# Revit family: 859-001X-001 DN350-600 final
name_source: partatom
category: Pipe Accessories
units: mm (PartAtom-declared; Revit-internal decimal feet)

## family parameters
Always vertical = Yes
Cut with Voids When Loaded = No
Part Type = Valve - Breaks Into
Round Connector Dimension = Use Diameter
Shared = No
Work Plane-Based = No

## types (35) — shared parameters
10 = 10 mm  [stored 0.0328084 ft]
131 = 131 mm
18 = 11 mm  [stored 0.0360892 ft]
3 = 3 mm  [stored 0.00984252 ft]
48 = 15 mm  [stored 0.0492126 ft]
50 = 50 mm
53 = 20 mm  [stored 0.0656168 ft]
8 = 8 mm  [stored 0.0262467 ft]
DN350_PN10_Pilot range ( 0.3 - 1.5) = 859-0350-00-0140018
DN350_PN10_Pilot range ( 1.5 - 6) = 859-0350-00-0140010
DN350_PN10_Pilot range ( 5 - 10) = 859-0350-00-0140011
DN350_PN16_Pilot range ( 0.3 - 1.5) = 859-0350-00-1140018
DN350_PN16_Pilot range ( 0.5 - 6) = 859-0350-00-1140010
DN350_PN16_Pilot range ( 10 - 16) = 859-0350-00-1140012
DN350_PN16_Pilot range ( 5 - 10) = 859-0350-00-1140011
DN400_PN10_Pilot range ( 0.3 - 1.5) = 859-0400-00-0140018
DN400_PN10_Pilot range ( 1.5 - 6) = 859-0400-00-0140010
DN400_PN10_Pilot range ( 5 - 10) = 859-0400-00-0140011
DN400_PN16_Pilot range ( 0.3 - 1.5) = 859-0400-00-1140018
DN400_PN16_Pilot range ( 1.5 - 6) = 859-0400-00-1140010
DN400_PN16_Pilot range ( 10 - 16) = 859-0400-00-1140012
DN400_PN16_Pilot range ( 5 - 10) = 859-0400-00-1140011
DN450_PN10_Pilot range ( 0.3 - 1.5) = 859-0450-00-0140018
DN450_PN10_Pilot range ( 1.5 - 6) = 859-0450-00-0140010
DN450_PN10_Pilot range ( 5 - 10) = 859-0450-00-0140011
DN450_PN16_Pilot range (  10 - 16) = 859-0450-00-1140012
DN450_PN16_Pilot range ( 0.3 - 1.5) = 859-0450-00-1140018
DN450_PN16_Pilot range ( 1.5 - 6) = 859-0450-00-1140010
DN450_PN16_Pilot range ( 5 - 10) = 859-0450-00-1140011
DN500_PN10_Pilot range ( 0.3 - 1.5) = 859-0500-00-0140018
DN500_PN10_Pilot range ( 1.5 - 6) = 859-0500-00-0140010
DN500_PN10_Pilot range ( 5 - 10) = 859-0500-00-0140011
DN500_PN16_Pilot range ( 0.3 - 1.5) = 859-0500-00-1140018
DN500_PN16_Pilot range ( 1.5 - 6) = 859-0500-00-1140010
DN500_PN16_Pilot range ( 10 - 16) = 859-0500-00-1140012
DN500_PN16_Pilot range ( 5 - 10) = 859-0500-00-1140011
DN600_PN10_Pilot range ( 0.3 - 1.5) = 859-0600-00-0140018
DN600_PN10_Pilot range ( 1.5 - 6) = 859-0600-00-0140010
DN600_PN10_Pilot range ( 5 - 10) = 859-0600-00-0140011
DN600_PN16_Pilot range ( 0.3 - 1.5) = 859-0600-00-1140018
DN600_PN16_Pilot range ( 1.5 - 6) = 859-0600-00-1140010
DN600_PN16_Pilot range ( 10 - 16) = 859-0600-00-1140012
DN600_PN16_Pilot range ( 5 - 10) = 859-0600-00-1140011
Description_ = AVK CONTROL VALVE, PRESSURE SUSTAINING/RELIEF, PN10/16
Search_table = 859-001X-001 DN350-600
URL_product_pages = https://www.avkvalves.com
zero-valued in all types: 0, Actuator, Default Elevation

## per-type parameters (varying)
- DN350_PN10_Pilot range ( 1.5 - 6): Actuator_L=136 mm; Actuator_L1=122 mm; Actuator_d=43 mm; Body_H=312 mm; Body_Rib_L=130 mm; Bolt_Dia=33 mm  [stored 0.108268 ft]; Bonnet_D=156 mm; Bonnet_D1=312 mm; Bonnet_R=328 mm; Bonnet_dim1=218 mm; Bonnet_dim1_H=22 mm; Bonnet_dim1_H1=445 mm; Bonnet_dim2=109 mm; Bonnet_dim3=82 mm; Bore=175 mm; Bore1=210 mm; Bore2=263 mm; Centre_D=70 mm; Centre_D1=56 mm; Centre_nut=53 mm; Conrol_dim.=186 mm; Control_dim1=16 mm  [stored 0.0524934 ft]; Control_dim2=98 mm; Control_dim3=8 mm  [stored 0.0262467 ft]; Control_dim4=281 mm; Control_dim5=22 mm; Control_dim6=27 mm; Control_dim7=36 mm  [stored 0.11811 ft]; D=260 mm; DN=350 mm; FL_T=25 mm  [stored 0.082021 ft]; H3=808 mm; H33=31 mm; H4=62 mm; L=980 mm; L3=360 mm; Nut_Dim1=42 mm; Nut_Dim2=7 mm  [stored 0.0229659 ft]; Nut_T=20 mm  [stored 0.0656168 ft]; Raised_R=34 mm; Raised_dis=4 mm  [stored 0.0131234 ft]; Sweep_R=19 mm  [stored 0.062336 ft]; Thickness=15 mm  [stored 0.0492126 ft]; Thickness1=18 mm  [stored 0.0590551 ft]; W=290 mm; W1=302 mm; W11=216 mm; W2=302 mm; W22=242 mm; Wd1=257 mm; Wd2=302 mm; centre=273 mm; dim1=121 mm; nut_dim=156 mm; sweep=28 mm  [stored 0.0918635 ft]; sweep/2=6 mm  [stored 0.019685 ft]; sweep1=13 mm; sweep_2=6 mm  [stored 0.019685 ft]; sweep_D=25 mm  [stored 0.082021 ft]; sweep_H=356 mm; sweep_H1=31 mm; sweep_box1=35 mm  [stored 0.114829 ft]; sweep_box2=16 mm  [stored 0.0524934 ft]
- DN350_PN10_Pilot range ( 5 - 10): Actuator_L=136 mm; Actuator_L1=122 mm; Actuator_d=43 mm; Body_H=312 mm; Body_Rib_L=130 mm; Bolt_Dia=33 mm  [stored 0.108268 ft]; Bonnet_D=156 mm; Bonnet_D1=312 mm; Bonnet_R=328 mm; Bonnet_dim1=218 mm; Bonnet_dim1_H=22 mm; Bonnet_dim1_H1=445 mm; Bonnet_dim2=109 mm; Bonnet_dim3=82 mm; Bore=175 mm; Bore1=210 mm; Bore2=263 mm; Centre_D=70 mm; Centre_D1=56 mm; Centre_nut=53 mm; Conrol_dim.=186 mm; Control_dim1=16 mm  [stored 0.0524934 ft]; Control_dim2=98 mm; Control_dim3=8 mm  [stored 0.0262467 ft]; Control_dim4=281 mm; Control_dim5=22 mm; Control_dim6=27 mm; Control_dim7=36 mm  [stored 0.11811 ft]; D=260 mm; DN=350 mm; FL_T=25 mm  [stored 0.082021 ft]; H3=808 mm; H33=31 mm; H4=62 mm; L=980 mm; L3=360 mm; Nut_Dim1=42 mm; Nut_Dim2=7 mm  [stored 0.0229659 ft]; Nut_T=20 mm  [stored 0.0656168 ft]; Raised_R=34 mm; Raised_dis=4 mm  [stored 0.0131234 ft]; Sweep_R=19 mm  [stored 0.062336 ft]; Thickness=15 mm  [stored 0.0492126 ft]; Thickness1=18 mm  [stored 0.0590551 ft]; W=290 mm; W1=302 mm; W11=216 mm; W2=302 mm; W22=242 mm; Wd1=257 mm; Wd2=302 mm; centre=273 mm; dim1=121 mm; nut_dim=156 mm; sweep=28 mm  [stored 0.0918635 ft]; sweep/2=6 mm  [stored 0.019685 ft]; sweep1=13 mm; sweep_2=6 mm  [stored 0.019685 ft]; sweep_D=25 mm  [stored 0.082021 ft]; sweep_H=356 mm; sweep_H1=31 mm; sweep_box1=35 mm  [stored 0.114829 ft]; sweep_box2=16 mm  [stored 0.0524934 ft]
- DN350_PN10_Pilot range ( 0.3 - 1.5): Actuator_L=136 mm; Actuator_L1=122 mm; Actuator_d=43 mm; Body_H=312 mm; Body_Rib_L=130 mm; Bolt_Dia=33 mm  [stored 0.108268 ft]; Bonnet_D=156 mm; Bonnet_D1=312 mm; Bonnet_R=328 mm; Bonnet_dim1=218 mm; Bonnet_dim1_H=22 mm; Bonnet_dim1_H1=445 mm; Bonnet_dim2=109 mm; Bonnet_dim3=82 mm; Bore=175 mm; Bore1=210 mm; Bore2=263 mm; Centre_D=70 mm; Centre_D1=56 mm; Centre_nut=53 mm; Conrol_dim.=186 mm; Control_dim1=16 mm  [stored 0.0524934 ft]; Control_dim2=98 mm; Control_dim3=8 mm  [stored 0.0262467 ft]; Control_dim4=281 mm; Control_dim5=22 mm; Control_dim6=27 mm; Control_dim7=36 mm  [stored 0.11811 ft]; D=260 mm; DN=350 mm; FL_T=25 mm  [stored 0.082021 ft]; H3=808 mm; H33=31 mm; H4=62 mm; L=980 mm; L3=360 mm; Nut_Dim1=42 mm; Nut_Dim2=7 mm  [stored 0.0229659 ft]; Nut_T=20 mm  [stored 0.0656168 ft]; Raised_R=34 mm; Raised_dis=4 mm  [stored 0.0131234 ft]; Sweep_R=19 mm  [stored 0.062336 ft]; Thickness=15 mm  [stored 0.0492126 ft]; Thickness1=18 mm  [stored 0.0590551 ft]; W=290 mm; W1=302 mm; W11=216 mm; W2=302 mm; W22=242 mm; Wd1=257 mm; Wd2=302 mm; centre=273 mm; dim1=121 mm; nut_dim=156 mm; sweep=28 mm  [stored 0.0918635 ft]; sweep/2=6 mm  [stored 0.019685 ft]; sweep1=13 mm; sweep_2=6 mm  [stored 0.019685 ft]; sweep_D=25 mm  [stored 0.082021 ft]; sweep_H=356 mm; sweep_H1=31 mm; sweep_box1=35 mm  [stored 0.114829 ft]; sweep_box2=16 mm  [stored 0.0524934 ft]
- DN350_PN16_Pilot range ( 0.5 - 6): Actuator_L=136 mm; Actuator_L1=122 mm; Actuator_d=43 mm; Body_H=312 mm; Body_Rib_L=130 mm; Bolt_Dia=33 mm  [stored 0.108268 ft]; Bonnet_D=156 mm; Bonnet_D1=312 mm; Bonnet_R=328 mm; Bonnet_dim1=218 mm; Bonnet_dim1_H=22 mm; Bonnet_dim1_H1=445 mm; Bonnet_dim2=109 mm; Bonnet_dim3=82 mm; Bore=175 mm; Bore1=210 mm; Bore2=263 mm; Centre_D=70 mm; Centre_D1=56 mm; Centre_nut=53 mm; Conrol_dim.=186 mm; Control_dim1=16 mm  [stored 0.0524934 ft]; Control_dim2=98 mm; Control_dim3=8 mm  [stored 0.0262467 ft]; Control_dim4=281 mm; Control_dim5=22 mm; Control_dim6=27 mm; Control_dim7=36 mm  [stored 0.11811 ft]; D=260 mm; DN=351 mm; FL_T=27 mm; H3=808 mm; H33=31 mm; H4=62 mm; L=980 mm; L3=360 mm; Nut_Dim1=42 mm; Nut_Dim2=7 mm  [stored 0.0229659 ft]; Nut_T=21 mm; Raised_R=34 mm; Raised_dis=4 mm  [stored 0.0131234 ft]; Sweep_R=19 mm  [stored 0.062336 ft]; Thickness=16 mm  [stored 0.0524934 ft]; Thickness1=19 mm  [stored 0.062336 ft]; W=290 mm; W1=302 mm; W11=216 mm; W2=302 mm; W22=242 mm; Wd1=257 mm; Wd2=302 mm; centre=273 mm; dim1=121 mm; nut_dim=156 mm; sweep=28 mm  [stored 0.0918635 ft]; sweep/2=6 mm  [stored 0.019685 ft]; sweep1=13 mm; sweep_2=6 mm  [stored 0.019685 ft]; sweep_D=25 mm  [stored 0.082021 ft]; sweep_H=356 mm; sweep_H1=31 mm; sweep_box1=35 mm  [stored 0.114829 ft]; sweep_box2=16 mm  [stored 0.0524934 ft]
- DN350_PN16_Pilot range ( 5 - 10): Actuator_L=136 mm; Actuator_L1=122 mm; Actuator_d=43 mm; Body_H=312 mm; Body_Rib_L=130 mm; Bolt_Dia=33 mm  [stored 0.108268 ft]; Bonnet_D=156 mm; Bonnet_D1=312 mm; Bonnet_R=328 mm; Bonnet_dim1=218 mm; Bonnet_dim1_H=22 mm; Bonnet_dim1_H1=445 mm; Bonnet_dim2=109 mm; Bonnet_dim3=82 mm; Bore=175 mm; Bore1=210 mm; Bore2=263 mm; Centre_D=70 mm; Centre_D1=56 mm; Centre_nut=53 mm; Conrol_dim.=186 mm; Control_dim1=16 mm  [stored 0.0524934 ft]; Control_dim2=98 mm; Control_dim3=8 mm  [stored 0.0262467 ft]; Control_dim4=281 mm; Control_dim5=22 mm; Control_dim6=27 mm; Control_dim7=36 mm  [stored 0.11811 ft]; D=260 mm; DN=351 mm; FL_T=27 mm; H3=808 mm; H33=31 mm; H4=62 mm; L=980 mm; L3=360 mm; Nut_Dim1=42 mm; Nut_Dim2=7 mm  [stored 0.0229659 ft]; Nut_T=21 mm; Raised_R=34 mm; Raised_dis=4 mm  [stored 0.0131234 ft]; Sweep_R=19 mm  [stored 0.062336 ft]; Thickness=16 mm  [stored 0.0524934 ft]; Thickness1=19 mm  [stored 0.062336 ft]; W=290 mm; W1=302 mm; W11=216 mm; W2=302 mm; W22=242 mm; Wd1=257 mm; Wd2=302 mm; centre=274 mm; dim1=121 mm; nut_dim=156 mm; sweep=28 mm  [stored 0.0918635 ft]; sweep/2=6 mm  [stored 0.019685 ft]; sweep1=13 mm; sweep_2=6 mm  [stored 0.019685 ft]; sweep_D=25 mm  [stored 0.082021 ft]; sweep_H=356 mm; sweep_H1=31 mm; sweep_box1=35 mm  [stored 0.114829 ft]; sweep_box2=16 mm  [stored 0.0524934 ft]
- DN350_PN16_Pilot range ( 10 - 16): Actuator_L=136 mm; Actuator_L1=122 mm; Actuator_d=43 mm; Body_H=312 mm; Body_Rib_L=130 mm; Bolt_Dia=33 mm  [stored 0.108268 ft]; Bonnet_D=156 mm; Bonnet_D1=312 mm; Bonnet_R=328 mm; Bonnet_dim1=218 mm; Bonnet_dim1_H=22 mm; Bonnet_dim1_H1=445 mm; Bonnet_dim2=109 mm; Bonnet_dim3=82 mm; Bore=175 mm; Bore1=210 mm; Bore2=263 mm; Centre_D=70 mm; Centre_D1=56 mm; Centre_nut=53 mm; Conrol_dim.=186 mm; Control_dim1=16 mm  [stored 0.0524934 ft]; Control_dim2=98 mm; Control_dim3=8 mm  [stored 0.0262467 ft]; Control_dim4=281 mm; Control_dim5=22 mm; Control_dim6=27 mm; Control_dim7=36 mm  [stored 0.11811 ft]; D=260 mm; DN=351 mm; FL_T=27 mm; H3=808 mm; H33=31 mm; H4=62 mm; L=980 mm; L3=360 mm; Nut_Dim1=42 mm; Nut_Dim2=7 mm  [stored 0.0229659 ft]; Nut_T=21 mm; Raised_R=34 mm; Raised_dis=4 mm  [stored 0.0131234 ft]; Sweep_R=19 mm  [stored 0.062336 ft]; Thickness=16 mm  [stored 0.0524934 ft]; Thickness1=19 mm  [stored 0.062336 ft]; W=290 mm; W1=302 mm; W11=216 mm; W2=302 mm; W22=242 mm; Wd1=257 mm; Wd2=302 mm; centre=273 mm; dim1=121 mm; nut_dim=156 mm; sweep=28 mm  [stored 0.0918635 ft]; sweep/2=6 mm  [stored 0.019685 ft]; sweep1=13 mm; sweep_2=6 mm  [stored 0.019685 ft]; sweep_D=25 mm  [stored 0.082021 ft]; sweep_H=356 mm; sweep_H1=31 mm; sweep_box1=35 mm  [stored 0.114829 ft]; sweep_box2=16 mm  [stored 0.0524934 ft]
- DN350_PN16_Pilot range ( 0.3 - 1.5): Actuator_L=136 mm; Actuator_L1=122 mm; Actuator_d=43 mm; Body_H=312 mm; Body_Rib_L=130 mm; Bolt_Dia=33 mm  [stored 0.108268 ft]; Bonnet_D=156 mm; Bonnet_D1=312 mm; Bonnet_R=328 mm; Bonnet_dim1=218 mm; Bonnet_dim1_H=22 mm; Bonnet_dim1_H1=445 mm; Bonnet_dim2=109 mm; Bonnet_dim3=82 mm; Bore=175 mm; Bore1=210 mm; Bore2=263 mm; Centre_D=70 mm; Centre_D1=56 mm; Centre_nut=53 mm; Conrol_dim.=186 mm; Control_dim1=16 mm  [stored 0.0524934 ft]; Control_dim2=98 mm; Control_dim3=8 mm  [stored 0.0262467 ft]; Control_dim4=281 mm; Control_dim5=22 mm; Control_dim6=27 mm; Control_dim7=36 mm  [stored 0.11811 ft]; D=260 mm; DN=350 mm; FL_T=27 mm; H3=808 mm; H33=31 mm; H4=62 mm; L=980 mm; L3=360 mm; Nut_Dim1=42 mm; Nut_Dim2=7 mm  [stored 0.0229659 ft]; Nut_T=21 mm; Raised_R=34 mm; Raised_dis=4 mm  [stored 0.0131234 ft]; Sweep_R=19 mm  [stored 0.062336 ft]; Thickness=16 mm  [stored 0.0524934 ft]; Thickness1=19 mm  [stored 0.062336 ft]; W=290 mm; W1=302 mm; W11=216 mm; W2=302 mm; W22=242 mm; Wd1=257 mm; Wd2=302 mm; centre=273 mm; dim1=121 mm; nut_dim=156 mm; sweep=28 mm  [stored 0.0918635 ft]; sweep/2=6 mm  [stored 0.019685 ft]; sweep1=13 mm; sweep_2=6 mm  [stored 0.019685 ft]; sweep_D=25 mm  [stored 0.082021 ft]; sweep_H=356 mm; sweep_H1=31 mm; sweep_box1=35 mm  [stored 0.114829 ft]; sweep_box2=16 mm  [stored 0.0524934 ft]
- DN400_PN10_Pilot range ( 1.5 - 6): Actuator_L=160 mm; Actuator_L1=144 mm; Actuator_d=48 mm; Body_H=348 mm; Body_Rib_L=145 mm; Bolt_Dia=39 mm  [stored 0.127953 ft]; Bonnet_D=174 mm; Bonnet_D1=348 mm; Bonnet_R=365 mm; Bonnet_dim1=244 mm; Bonnet_dim1_H=35 mm  [stored 0.114829 ft]; Bonnet_dim1_H1=522 mm; Bonnet_dim2=122 mm; Bonnet_dim3=91 mm; Bore=200 mm; Bore1=240 mm; Bore2=300 mm; Centre_D=80 mm; Centre_D1=64 mm; Centre_nut=60 mm; Conrol_dim.=207 mm; Control_dim1=18 mm  [stored 0.0590551 ft]; Control_dim2=110 mm; Control_dim3=9 mm; Control_dim4=313 mm; Control_dim5=25 mm  [stored 0.082021 ft]; Control_dim6=30 mm  [stored 0.0984252 ft]; Control_dim7=40 mm  [stored 0.131234 ft]; D=290 mm; DN=400 mm; FL_T=25 mm  [stored 0.082021 ft]; H3=932 mm; H33=36 mm  [stored 0.11811 ft]; H4=72 mm; L=1100 mm; L3=402 mm; Nut_Dim1=51 mm; Nut_Dim2=7 mm  [stored 0.0229659 ft]; Nut_T=20 mm  [stored 0.0656168 ft]; Raised_R=36 mm  [stored 0.11811 ft]; Raised_dis=4 mm  [stored 0.0131234 ft]; Sweep_R=23 mm; Thickness=15 mm  [stored 0.0492126 ft]; Thickness1=18 mm  [stored 0.0590551 ft]; W=340 mm; W1=355 mm; W11=254 mm; W2=355 mm; W22=284 mm; Wd1=302 mm; Wd2=343 mm; centre=312 mm; dim1=142 mm; nut_dim=174 mm; sweep=33 mm  [stored 0.108268 ft]; sweep/2=8 mm  [stored 0.0262467 ft]; sweep1=15 mm  [stored 0.0492126 ft]; sweep_2=8 mm  [stored 0.0262467 ft]; sweep_D=30 mm  [stored 0.0984252 ft]; sweep_H=417 mm; sweep_H1=49 mm; sweep_box1=40 mm  [stored 0.131234 ft]; sweep_box2=20 mm  [stored 0.0656168 ft]
- DN400_PN10_Pilot range ( 5 - 10): Actuator_L=160 mm; Actuator_L1=144 mm; Actuator_d=48 mm; Body_H=348 mm; Body_Rib_L=145 mm; Bolt_Dia=39 mm  [stored 0.127953 ft]; Bonnet_D=174 mm; Bonnet_D1=348 mm; Bonnet_R=365 mm; Bonnet_dim1=244 mm; Bonnet_dim1_H=35 mm  [stored 0.114829 ft]; Bonnet_dim1_H1=522 mm; Bonnet_dim2=122 mm; Bonnet_dim3=91 mm; Bore=200 mm; Bore1=240 mm; Bore2=300 mm; Centre_D=80 mm; Centre_D1=64 mm; Centre_nut=60 mm; Conrol_dim.=207 mm; Control_dim1=18 mm  [stored 0.0590551 ft]; Control_dim2=110 mm; Control_dim3=9 mm; Control_dim4=313 mm; Control_dim5=25 mm  [stored 0.082021 ft]; Control_dim6=30 mm  [stored 0.0984252 ft]; Control_dim7=40 mm  [stored 0.131234 ft]; D=290 mm; DN=400 mm; FL_T=25 mm  [stored 0.082021 ft]; H3=932 mm; H33=36 mm  [stored 0.11811 ft]; H4=72 mm; L=1100 mm; L3=402 mm; Nut_Dim1=51 mm; Nut_Dim2=7 mm  [stored 0.0229659 ft]; Nut_T=20 mm  [stored 0.0656168 ft]; Raised_R=36 mm  [stored 0.11811 ft]; Raised_dis=4 mm  [stored 0.0131234 ft]; Sweep_R=23 mm; Thickness=15 mm  [stored 0.0492126 ft]; Thickness1=18 mm  [stored 0.0590551 ft]; W=340 mm; W1=355 mm; W11=254 mm; W2=355 mm; W22=284 mm; Wd1=302 mm; Wd2=343 mm; centre=312 mm; dim1=142 mm; nut_dim=174 mm; sweep=33 mm  [stored 0.108268 ft]; sweep/2=8 mm  [stored 0.0262467 ft]; sweep1=15 mm  [stored 0.0492126 ft]; sweep_2=8 mm  [stored 0.0262467 ft]; sweep_D=30 mm  [stored 0.0984252 ft]; sweep_H=417 mm; sweep_H1=49 mm; sweep_box1=40 mm  [stored 0.131234 ft]; sweep_box2=20 mm  [stored 0.0656168 ft]
- DN400_PN10_Pilot range ( 0.3 - 1.5): Actuator_L=160 mm; Actuator_L1=144 mm; Actuator_d=48 mm; Body_H=348 mm; Body_Rib_L=145 mm; Bolt_Dia=39 mm  [stored 0.127953 ft]; Bonnet_D=174 mm; Bonnet_D1=348 mm; Bonnet_R=365 mm; Bonnet_dim1=244 mm; Bonnet_dim1_H=35 mm  [stored 0.114829 ft]; Bonnet_dim1_H1=522 mm; Bonnet_dim2=122 mm; Bonnet_dim3=91 mm; Bore=200 mm; Bore1=240 mm; Bore2=300 mm; Centre_D=80 mm; Centre_D1=64 mm; Centre_nut=60 mm; Conrol_dim.=207 mm; Control_dim1=18 mm  [stored 0.0590551 ft]; Control_dim2=110 mm; Control_dim3=9 mm; Control_dim4=313 mm; Control_dim5=25 mm  [stored 0.082021 ft]; Control_dim6=30 mm  [stored 0.0984252 ft]; Control_dim7=40 mm  [stored 0.131234 ft]; D=290 mm; DN=400 mm; FL_T=25 mm  [stored 0.082021 ft]; H3=932 mm; H33=36 mm  [stored 0.11811 ft]; H4=72 mm; L=1100 mm; L3=402 mm; Nut_Dim1=51 mm; Nut_Dim2=7 mm  [stored 0.0229659 ft]; Nut_T=20 mm  [stored 0.0656168 ft]; Raised_R=36 mm  [stored 0.11811 ft]; Raised_dis=4 mm  [stored 0.0131234 ft]; Sweep_R=23 mm; Thickness=15 mm  [stored 0.0492126 ft]; Thickness1=18 mm  [stored 0.0590551 ft]; W=340 mm; W1=355 mm; W11=254 mm; W2=355 mm; W22=284 mm; Wd1=302 mm; Wd2=343 mm; centre=312 mm; dim1=142 mm; nut_dim=174 mm; sweep=33 mm  [stored 0.108268 ft]; sweep/2=8 mm  [stored 0.0262467 ft]; sweep1=15 mm  [stored 0.0492126 ft]; sweep_2=8 mm  [stored 0.0262467 ft]; sweep_D=30 mm  [stored 0.0984252 ft]; sweep_H=417 mm; sweep_H1=49 mm; sweep_box1=40 mm  [stored 0.131234 ft]; sweep_box2=20 mm  [stored 0.0656168 ft]
- DN400_PN16_Pilot range ( 1.5 - 6): Actuator_L=160 mm; Actuator_L1=144 mm; Actuator_d=48 mm; Body_H=348 mm; Body_Rib_L=145 mm; Bolt_Dia=39 mm  [stored 0.127953 ft]; Bonnet_D=174 mm; Bonnet_D1=348 mm; Bonnet_R=365 mm; Bonnet_dim1=244 mm; Bonnet_dim1_H=35 mm  [stored 0.114829 ft]; Bonnet_dim1_H1=522 mm; Bonnet_dim2=122 mm; Bonnet_dim3=91 mm; Bore=200 mm; Bore1=240 mm; Bore2=300 mm; Centre_D=80 mm; Centre_D1=64 mm; Centre_nut=60 mm; Conrol_dim.=207 mm; Control_dim1=18 mm  [stored 0.0590551 ft]; Control_dim2=110 mm; Control_dim3=9 mm; Control_dim4=313 mm; Control_dim5=25 mm  [stored 0.082021 ft]; Control_dim6=30 mm  [stored 0.0984252 ft]; Control_dim7=40 mm  [stored 0.131234 ft]; D=290 mm; DN=401 mm; FL_T=28 mm  [stored 0.0918635 ft]; H3=932 mm; H33=36 mm  [stored 0.11811 ft]; H4=72 mm; L=1100 mm; L3=402 mm; Nut_Dim1=51 mm; Nut_Dim2=7 mm  [stored 0.0229659 ft]; Nut_T=22 mm; Raised_R=36 mm  [stored 0.11811 ft]; Raised_dis=4 mm  [stored 0.0131234 ft]; Sweep_R=23 mm; Thickness=17 mm; Thickness1=20 mm  [stored 0.0656168 ft]; W=340 mm; W1=355 mm; W11=254 mm; W2=355 mm; W22=284 mm; Wd1=302 mm; Wd2=343 mm; centre=312 mm; dim1=142 mm; nut_dim=174 mm; sweep=33 mm  [stored 0.108268 ft]; sweep/2=8 mm  [stored 0.0262467 ft]; sweep1=15 mm  [stored 0.0492126 ft]; sweep_2=8 mm  [stored 0.0262467 ft]; sweep_D=30 mm  [stored 0.0984252 ft]; sweep_H=417 mm; sweep_H1=49 mm; sweep_box1=40 mm  [stored 0.131234 ft]; sweep_box2=20 mm  [stored 0.0656168 ft]
- DN400_PN16_Pilot range ( 5 - 10): Actuator_L=160 mm; Actuator_L1=144 mm; Actuator_d=48 mm; Body_H=348 mm; Body_Rib_L=145 mm; Bolt_Dia=39 mm  [stored 0.127953 ft]; Bonnet_D=174 mm; Bonnet_D1=348 mm; Bonnet_R=365 mm; Bonnet_dim1=244 mm; Bonnet_dim1_H=35 mm  [stored 0.114829 ft]; Bonnet_dim1_H1=522 mm; Bonnet_dim2=122 mm; Bonnet_dim3=91 mm; Bore=200 mm; Bore1=240 mm; Bore2=301 mm; Centre_D=80 mm; Centre_D1=64 mm; Centre_nut=60 mm; Conrol_dim.=207 mm; Control_dim1=18 mm  [stored 0.0590551 ft]; Control_dim2=110 mm; Control_dim3=9 mm; Control_dim4=313 mm; Control_dim5=25 mm  [stored 0.082021 ft]; Control_dim6=30 mm  [stored 0.0984252 ft]; Control_dim7=40 mm  [stored 0.131234 ft]; D=290 mm; DN=401 mm; FL_T=28 mm  [stored 0.0918635 ft]; H3=932 mm; H33=36 mm  [stored 0.11811 ft]; H4=72 mm; L=1100 mm; L3=402 mm; Nut_Dim1=51 mm; Nut_Dim2=7 mm  [stored 0.0229659 ft]; Nut_T=22 mm; Raised_R=36 mm  [stored 0.11811 ft]; Raised_dis=4 mm  [stored 0.0131234 ft]; Sweep_R=23 mm; Thickness=17 mm; Thickness1=20 mm  [stored 0.0656168 ft]; W=340 mm; W1=355 mm; W11=254 mm; W2=355 mm; W22=284 mm; Wd1=302 mm; Wd2=343 mm; centre=313 mm; dim1=142 mm; nut_dim=174 mm; sweep=33 mm  [stored 0.108268 ft]; sweep/2=8 mm  [stored 0.0262467 ft]; sweep1=15 mm  [stored 0.0492126 ft]; sweep_2=8 mm  [stored 0.0262467 ft]; sweep_D=30 mm  [stored 0.0984252 ft]; sweep_H=417 mm; sweep_H1=49 mm; sweep_box1=40 mm  [stored 0.131234 ft]; sweep_box2=20 mm  [stored 0.0656168 ft]
- DN400_PN16_Pilot range ( 10 - 16): Actuator_L=160 mm; Actuator_L1=144 mm; Actuator_d=48 mm; Body_H=348 mm; Body_Rib_L=145 mm; Bolt_Dia=39 mm  [stored 0.127953 ft]; Bonnet_D=174 mm; Bonnet_D1=348 mm; Bonnet_R=365 mm; Bonnet_dim1=244 mm; Bonnet_dim1_H=35 mm  [stored 0.114829 ft]; Bonnet_dim1_H1=522 mm; Bonnet_dim2=122 mm; Bonnet_dim3=91 mm; Bore=200 mm; Bore1=240 mm; Bore2=300 mm; Centre_D=80 mm; Centre_D1=64 mm; Centre_nut=60 mm; Conrol_dim.=207 mm; Control_dim1=18 mm  [stored 0.0590551 ft]; Control_dim2=110 mm; Control_dim3=9 mm; Control_dim4=313 mm; Control_dim5=25 mm  [stored 0.082021 ft]; Control_dim6=30 mm  [stored 0.0984252 ft]; Control_dim7=40 mm  [stored 0.131234 ft]; D=290 mm; DN=401 mm; FL_T=28 mm  [stored 0.0918635 ft]; H3=932 mm; H33=36 mm  [stored 0.11811 ft]; H4=72 mm; L=1100 mm; L3=402 mm; Nut_Dim1=51 mm; Nut_Dim2=7 mm  [stored 0.0229659 ft]; Nut_T=22 mm; Raised_R=36 mm  [stored 0.11811 ft]; Raised_dis=4 mm  [stored 0.0131234 ft]; Sweep_R=23 mm; Thickness=17 mm; Thickness1=20 mm  [stored 0.0656168 ft]; W=340 mm; W1=355 mm; W11=254 mm; W2=355 mm; W22=284 mm; Wd1=302 mm; Wd2=343 mm; centre=312 mm; dim1=142 mm; nut_dim=174 mm; sweep=33 mm  [stored 0.108268 ft]; sweep/2=8 mm  [stored 0.0262467 ft]; sweep1=15 mm  [stored 0.0492126 ft]; sweep_2=8 mm  [stored 0.0262467 ft]; sweep_D=30 mm  [stored 0.0984252 ft]; sweep_H=417 mm; sweep_H1=49 mm; sweep_box1=40 mm  [stored 0.131234 ft]; sweep_box2=20 mm  [stored 0.0656168 ft]
- DN400_PN16_Pilot range ( 0.3 - 1.5): Actuator_L=160 mm; Actuator_L1=144 mm; Actuator_d=48 mm; Body_H=348 mm; Body_Rib_L=145 mm; Bolt_Dia=39 mm  [stored 0.127953 ft]; Bonnet_D=174 mm; Bonnet_D1=348 mm; Bonnet_R=365 mm; Bonnet_dim1=244 mm; Bonnet_dim1_H=35 mm  [stored 0.114829 ft]; Bonnet_dim1_H1=522 mm; Bonnet_dim2=122 mm; Bonnet_dim3=91 mm; Bore=200 mm; Bore1=240 mm; Bore2=300 mm; Centre_D=80 mm; Centre_D1=64 mm; Centre_nut=60 mm; Conrol_dim.=207 mm; Control_dim1=18 mm  [stored 0.0590551 ft]; Control_dim2=110 mm; Control_dim3=9 mm; Control_dim4=313 mm; Control_dim5=25 mm  [stored 0.082021 ft]; Control_dim6=30 mm  [stored 0.0984252 ft]; Control_dim7=40 mm  [stored 0.131234 ft]; D=290 mm; DN=400 mm; FL_T=28 mm  [stored 0.0918635 ft]; H3=932 mm; H33=36 mm  [stored 0.11811 ft]; H4=72 mm; L=1100 mm; L3=402 mm; Nut_Dim1=51 mm; Nut_Dim2=7 mm  [stored 0.0229659 ft]; Nut_T=22 mm; Raised_R=36 mm  [stored 0.11811 ft]; Raised_dis=4 mm  [stored 0.0131234 ft]; Sweep_R=23 mm; Thickness=17 mm; Thickness1=20 mm  [stored 0.0656168 ft]; W=340 mm; W1=355 mm; W11=254 mm; W2=355 mm; W22=284 mm; Wd1=302 mm; Wd2=343 mm; centre=312 mm; dim1=142 mm; nut_dim=174 mm; sweep=33 mm  [stored 0.108268 ft]; sweep/2=8 mm  [stored 0.0262467 ft]; sweep1=15 mm  [stored 0.0492126 ft]; sweep_2=8 mm  [stored 0.0262467 ft]; sweep_D=30 mm  [stored 0.0984252 ft]; sweep_H=417 mm; sweep_H1=49 mm; sweep_box1=40 mm  [stored 0.131234 ft]; sweep_box2=20 mm  [stored 0.0656168 ft]
- DN450_PN10_Pilot range ( 1.5 - 6): Actuator_L=179 mm; Actuator_L1=161 mm; Actuator_d=53 mm; Body_H=384 mm; Body_Rib_L=160 mm; Bolt_Dia=39 mm  [stored 0.127953 ft]; Bonnet_D=192 mm; Bonnet_D1=384 mm; Bonnet_R=403 mm; Bonnet_dim1=269 mm; Bonnet_dim1_H=28 mm  [stored 0.0918635 ft]; Bonnet_dim1_H1=551 mm; Bonnet_dim2=134 mm; Bonnet_dim3=101 mm; Bore=225 mm; Bore1=270 mm; Bore2=338 mm; Centre_D=90 mm; Centre_D1=72 mm; Centre_nut=68 mm; Conrol_dim.=228 mm; Control_dim1=20 mm  [stored 0.0656168 ft]; Control_dim2=121 mm; Control_dim3=10 mm  [stored 0.0328084 ft]; Control_dim4=346 mm; Control_dim5=27 mm; Control_dim6=33 mm  [stored 0.108268 ft]; Control_dim7=44 mm; D=320 mm; DN=450 mm; FL_T=26 mm; H3=998 mm; H33=38 mm; H4=76 mm; L=1200 mm; L3=444 mm; Nut_Dim1=51 mm; Nut_Dim2=8 mm  [stored 0.0262467 ft]; Nut_T=20 mm  [stored 0.0656168 ft]; Raised_R=38 mm; Raised_dis=4 mm  [stored 0.0131234 ft]; Sweep_R=23 mm; Thickness=15 mm  [stored 0.0492126 ft]; Thickness1=18 mm  [stored 0.0590551 ft]; W=383 mm; W1=398 mm; W11=287 mm; W2=398 mm; W22=318 mm; Wd1=338 mm; Wd2=398 mm; centre=351 mm; dim1=159 mm; nut_dim=192 mm; sweep=33 mm  [stored 0.108268 ft]; sweep/2=8 mm  [stored 0.0262467 ft]; sweep1=15 mm  [stored 0.0492126 ft]; sweep_2=8 mm  [stored 0.0262467 ft]; sweep_D=30 mm  [stored 0.0984252 ft]; sweep_H=441 mm; sweep_H1=40 mm  [stored 0.131234 ft]; sweep_box1=45 mm; sweep_box2=20 mm  [stored 0.0656168 ft]
- DN450_PN10_Pilot range ( 5 - 10): Actuator_L=179 mm; Actuator_L1=161 mm; Actuator_d=53 mm; Body_H=384 mm; Body_Rib_L=160 mm; Bolt_Dia=39 mm  [stored 0.127953 ft]; Bonnet_D=192 mm; Bonnet_D1=384 mm; Bonnet_R=403 mm; Bonnet_dim1=269 mm; Bonnet_dim1_H=28 mm  [stored 0.0918635 ft]; Bonnet_dim1_H1=551 mm; Bonnet_dim2=134 mm; Bonnet_dim3=101 mm; Bore=225 mm; Bore1=270 mm; Bore2=338 mm; Centre_D=90 mm; Centre_D1=72 mm; Centre_nut=68 mm; Conrol_dim.=228 mm; Control_dim1=20 mm  [stored 0.0656168 ft]; Control_dim2=121 mm; Control_dim3=10 mm  [stored 0.0328084 ft]; Control_dim4=346 mm; Control_dim5=27 mm; Control_dim6=33 mm  [stored 0.108268 ft]; Control_dim7=44 mm; D=320 mm; DN=450 mm; FL_T=26 mm; H3=998 mm; H33=38 mm; H4=76 mm; L=1200 mm; L3=444 mm; Nut_Dim1=51 mm; Nut_Dim2=8 mm  [stored 0.0262467 ft]; Nut_T=20 mm  [stored 0.0656168 ft]; Raised_R=38 mm; Raised_dis=4 mm  [stored 0.0131234 ft]; Sweep_R=23 mm; Thickness=15 mm  [stored 0.0492126 ft]; Thickness1=18 mm  [stored 0.0590551 ft]; W=383 mm; W1=398 mm; W11=287 mm; W2=398 mm; W22=318 mm; Wd1=338 mm; Wd2=398 mm; centre=351 mm; dim1=159 mm; nut_dim=192 mm; sweep=33 mm  [stored 0.108268 ft]; sweep/2=8 mm  [stored 0.0262467 ft]; sweep1=15 mm  [stored 0.0492126 ft]; sweep_2=8 mm  [stored 0.0262467 ft]; sweep_D=30 mm  [stored 0.0984252 ft]; sweep_H=441 mm; sweep_H1=40 mm  [stored 0.131234 ft]; sweep_box1=45 mm; sweep_box2=20 mm  [stored 0.0656168 ft]
- DN450_PN10_Pilot range ( 0.3 - 1.5): Actuator_L=179 mm; Actuator_L1=161 mm; Actuator_d=53 mm; Body_H=384 mm; Body_Rib_L=160 mm; Bolt_Dia=39 mm  [stored 0.127953 ft]; Bonnet_D=192 mm; Bonnet_D1=384 mm; Bonnet_R=403 mm; Bonnet_dim1=269 mm; Bonnet_dim1_H=28 mm  [stored 0.0918635 ft]; Bonnet_dim1_H1=551 mm; Bonnet_dim2=134 mm; Bonnet_dim3=101 mm; Bore=225 mm; Bore1=270 mm; Bore2=338 mm; Centre_D=90 mm; Centre_D1=72 mm; Centre_nut=68 mm; Conrol_dim.=228 mm; Control_dim1=20 mm  [stored 0.0656168 ft]; Control_dim2=121 mm; Control_dim3=10 mm  [stored 0.0328084 ft]; Control_dim4=346 mm; Control_dim5=27 mm; Control_dim6=33 mm  [stored 0.108268 ft]; Control_dim7=44 mm; D=320 mm; DN=450 mm; FL_T=26 mm; H3=998 mm; H33=38 mm; H4=76 mm; L=1200 mm; L3=444 mm; Nut_Dim1=51 mm; Nut_Dim2=8 mm  [stored 0.0262467 ft]; Nut_T=20 mm  [stored 0.0656168 ft]; Raised_R=38 mm; Raised_dis=4 mm  [stored 0.0131234 ft]; Sweep_R=23 mm; Thickness=15 mm  [stored 0.0492126 ft]; Thickness1=18 mm  [stored 0.0590551 ft]; W=383 mm; W1=398 mm; W11=287 mm; W2=398 mm; W22=318 mm; Wd1=338 mm; Wd2=398 mm; centre=351 mm; dim1=159 mm; nut_dim=192 mm; sweep=33 mm  [stored 0.108268 ft]; sweep/2=8 mm  [stored 0.0262467 ft]; sweep1=15 mm  [stored 0.0492126 ft]; sweep_2=8 mm  [stored 0.0262467 ft]; sweep_D=30 mm  [stored 0.0984252 ft]; sweep_H=441 mm; sweep_H1=40 mm  [stored 0.131234 ft]; sweep_box1=45 mm; sweep_box2=20 mm  [stored 0.0656168 ft]
- DN450_PN16_Pilot range ( 1.5 - 6): Actuator_L=179 mm; Actuator_L1=161 mm; Actuator_d=53 mm; Body_H=384 mm; Body_Rib_L=160 mm; Bolt_Dia=39 mm  [stored 0.127953 ft]; Bonnet_D=192 mm; Bonnet_D1=384 mm; Bonnet_R=403 mm; Bonnet_dim1=269 mm; Bonnet_dim1_H=28 mm  [stored 0.0918635 ft]; Bonnet_dim1_H1=551 mm; Bonnet_dim2=134 mm; Bonnet_dim3=101 mm; Bore=225 mm; Bore1=270 mm; Bore2=338 mm; Centre_D=90 mm; Centre_D1=72 mm; Centre_nut=68 mm; Conrol_dim.=228 mm; Control_dim1=20 mm  [stored 0.0656168 ft]; Control_dim2=121 mm; Control_dim3=10 mm  [stored 0.0328084 ft]; Control_dim4=346 mm; Control_dim5=27 mm; Control_dim6=33 mm  [stored 0.108268 ft]; Control_dim7=44 mm; D=320 mm; DN=451 mm; FL_T=30 mm  [stored 0.0984252 ft]; H3=998 mm; H33=38 mm; H4=76 mm; L=1200 mm; L3=444 mm; Nut_Dim1=51 mm; Nut_Dim2=8 mm  [stored 0.0262467 ft]; Nut_T=24 mm  [stored 0.0787402 ft]; Raised_R=38 mm; Raised_dis=4 mm  [stored 0.0131234 ft]; Sweep_R=23 mm; Thickness=18 mm  [stored 0.0590551 ft]; Thickness1=22 mm; W=383 mm; W1=398 mm; W11=287 mm; W2=398 mm; W22=318 mm; Wd1=338 mm; Wd2=398 mm; centre=351 mm; dim1=159 mm; nut_dim=192 mm; sweep=33 mm  [stored 0.108268 ft]; sweep/2=8 mm  [stored 0.0262467 ft]; sweep1=15 mm  [stored 0.0492126 ft]; sweep_2=8 mm  [stored 0.0262467 ft]; sweep_D=30 mm  [stored 0.0984252 ft]; sweep_H=441 mm; sweep_H1=40 mm  [stored 0.131234 ft]; sweep_box1=45 mm; sweep_box2=20 mm  [stored 0.0656168 ft]
- DN450_PN16_Pilot range ( 5 - 10): Actuator_L=179 mm; Actuator_L1=161 mm; Actuator_d=53 mm; Body_H=384 mm; Body_Rib_L=160 mm; Bolt_Dia=39 mm  [stored 0.127953 ft]; Bonnet_D=192 mm; Bonnet_D1=384 mm; Bonnet_R=403 mm; Bonnet_dim1=269 mm; Bonnet_dim1_H=28 mm  [stored 0.0918635 ft]; Bonnet_dim1_H1=551 mm; Bonnet_dim2=134 mm; Bonnet_dim3=101 mm; Bore=225 mm; Bore1=270 mm; Bore2=338 mm; Centre_D=90 mm; Centre_D1=72 mm; Centre_nut=68 mm; Conrol_dim.=228 mm; Control_dim1=20 mm  [stored 0.0656168 ft]; Control_dim2=121 mm; Control_dim3=10 mm  [stored 0.0328084 ft]; Control_dim4=346 mm; Control_dim5=27 mm; Control_dim6=33 mm  [stored 0.108268 ft]; Control_dim7=44 mm; D=320 mm; DN=451 mm; FL_T=30 mm  [stored 0.0984252 ft]; H3=998 mm; H33=38 mm; H4=76 mm; L=1200 mm; L3=444 mm; Nut_Dim1=51 mm; Nut_Dim2=8 mm  [stored 0.0262467 ft]; Nut_T=24 mm  [stored 0.0787402 ft]; Raised_R=38 mm; Raised_dis=4 mm  [stored 0.0131234 ft]; Sweep_R=23 mm; Thickness=18 mm  [stored 0.0590551 ft]; Thickness1=22 mm; W=383 mm; W1=398 mm; W11=287 mm; W2=398 mm; W22=318 mm; Wd1=338 mm; Wd2=398 mm; centre=352 mm; dim1=159 mm; nut_dim=192 mm; sweep=33 mm  [stored 0.108268 ft]; sweep/2=8 mm  [stored 0.0262467 ft]; sweep1=15 mm  [stored 0.0492126 ft]; sweep_2=8 mm  [stored 0.0262467 ft]; sweep_D=30 mm  [stored 0.0984252 ft]; sweep_H=441 mm; sweep_H1=40 mm  [stored 0.131234 ft]; sweep_box1=45 mm; sweep_box2=20 mm  [stored 0.0656168 ft]
- DN450_PN16_Pilot range (  10 - 16): Actuator_L=179 mm; Actuator_L1=161 mm; Actuator_d=53 mm; Body_H=384 mm; Body_Rib_L=160 mm; Bolt_Dia=39 mm  [stored 0.127953 ft]; Bonnet_D=192 mm; Bonnet_D1=384 mm; Bonnet_R=403 mm; Bonnet_dim1=269 mm; Bonnet_dim1_H=28 mm  [stored 0.0918635 ft]; Bonnet_dim1_H1=551 mm; Bonnet_dim2=134 mm; Bonnet_dim3=101 mm; Bore=225 mm; Bore1=270 mm; Bore2=338 mm; Centre_D=90 mm; Centre_D1=72 mm; Centre_nut=68 mm; Conrol_dim.=228 mm; Control_dim1=20 mm  [stored 0.0656168 ft]; Control_dim2=121 mm; Control_dim3=10 mm  [stored 0.0328084 ft]; Control_dim4=346 mm; Control_dim5=27 mm; Control_dim6=33 mm  [stored 0.108268 ft]; Control_dim7=44 mm; D=320 mm; DN=450 mm; FL_T=30 mm  [stored 0.0984252 ft]; H3=998 mm; H33=38 mm; H4=76 mm; L=1200 mm; L3=444 mm; Nut_Dim1=51 mm; Nut_Dim2=8 mm  [stored 0.0262467 ft]; Nut_T=24 mm  [stored 0.0787402 ft]; Raised_R=38 mm; Raised_dis=4 mm  [stored 0.0131234 ft]; Sweep_R=23 mm; Thickness=18 mm  [stored 0.0590551 ft]; Thickness1=22 mm; W=383 mm; W1=398 mm; W11=287 mm; W2=398 mm; W22=318 mm; Wd1=338 mm; Wd2=398 mm; centre=351 mm; dim1=159 mm; nut_dim=192 mm; sweep=33 mm  [stored 0.108268 ft]; sweep/2=8 mm  [stored 0.0262467 ft]; sweep1=15 mm  [stored 0.0492126 ft]; sweep_2=8 mm  [stored 0.0262467 ft]; sweep_D=30 mm  [stored 0.0984252 ft]; sweep_H=441 mm; sweep_H1=40 mm  [stored 0.131234 ft]; sweep_box1=45 mm; sweep_box2=20 mm  [stored 0.0656168 ft]
- DN450_PN16_Pilot range ( 0.3 - 1.5): Actuator_L=179 mm; Actuator_L1=161 mm; Actuator_d=53 mm; Body_H=384 mm; Body_Rib_L=160 mm; Bolt_Dia=39 mm  [stored 0.127953 ft]; Bonnet_D=192 mm; Bonnet_D1=384 mm; Bonnet_R=403 mm; Bonnet_dim1=269 mm; Bonnet_dim1_H=28 mm  [stored 0.0918635 ft]; Bonnet_dim1_H1=551 mm; Bonnet_dim2=134 mm; Bonnet_dim3=101 mm; Bore=225 mm; Bore1=270 mm; Bore2=338 mm; Centre_D=90 mm; Centre_D1=72 mm; Centre_nut=68 mm; Conrol_dim.=228 mm; Control_dim1=20 mm  [stored 0.0656168 ft]; Control_dim2=121 mm; Control_dim3=10 mm  [stored 0.0328084 ft]; Control_dim4=346 mm; Control_dim5=27 mm; Control_dim6=33 mm  [stored 0.108268 ft]; Control_dim7=44 mm; D=320 mm; DN=451 mm; FL_T=30 mm  [stored 0.0984252 ft]; H3=998 mm; H33=38 mm; H4=76 mm; L=1200 mm; L3=444 mm; Nut_Dim1=51 mm; Nut_Dim2=8 mm  [stored 0.0262467 ft]; Nut_T=24 mm  [stored 0.0787402 ft]; Raised_R=38 mm; Raised_dis=4 mm  [stored 0.0131234 ft]; Sweep_R=23 mm; Thickness=18 mm  [stored 0.0590551 ft]; Thickness1=22 mm; W=383 mm; W1=398 mm; W11=287 mm; W2=398 mm; W22=318 mm; Wd1=338 mm; Wd2=398 mm; centre=351 mm; dim1=159 mm; nut_dim=192 mm; sweep=33 mm  [stored 0.108268 ft]; sweep/2=8 mm  [stored 0.0262467 ft]; sweep1=15 mm  [stored 0.0492126 ft]; sweep_2=8 mm  [stored 0.0262467 ft]; sweep_D=30 mm  [stored 0.0984252 ft]; sweep_H=441 mm; sweep_H1=40 mm  [stored 0.131234 ft]; sweep_box1=45 mm; sweep_box2=20 mm  [stored 0.0656168 ft]
- DN500_PN10_Pilot range ( 1.5 - 6): Actuator_L=209 mm; Actuator_L1=188 mm; Actuator_d=59 mm; Body_H=429 mm; Body_Rib_L=179 mm; Bolt_Dia=44 mm; Bonnet_D=215 mm; Bonnet_D1=429 mm; Bonnet_R=450 mm; Bonnet_dim1=300 mm; Bonnet_dim1_H=53 mm; Bonnet_dim1_H1=669 mm; Bonnet_dim2=150 mm; Bonnet_dim3=113 mm; Bore=250 mm; Bore1=300 mm; Bore2=375 mm; Centre_D=100 mm; Centre_D1=80 mm; Centre_nut=75 mm; Conrol_dim.=255 mm; Control_dim1=23 mm; Control_dim2=135 mm; Control_dim3=11 mm  [stored 0.0360892 ft]; Control_dim4=386 mm; Control_dim5=30 mm  [stored 0.0984252 ft]; Control_dim6=36 mm  [stored 0.11811 ft]; Control_dim7=49 mm; D=358 mm; DN=500 mm; FL_T=27 mm; H3=1181 mm; H33=46 mm; H4=93 mm; L=1250 mm; L3=495 mm; Nut_Dim1=57 mm; Nut_Dim2=9 mm; Nut_T=21 mm; Raised_R=43 mm; Raised_dis=4 mm  [stored 0.0131234 ft]; Sweep_R=26 mm; Thickness=16 mm  [stored 0.0524934 ft]; Thickness1=19 mm  [stored 0.062336 ft]; W=448 mm; W1=465 mm; W11=336 mm; W2=465 mm; W22=372 mm; Wd1=395 mm; Wd2=465 mm; centre=390 mm; dim1=186 mm; nut_dim=215 mm; sweep=37 mm; sweep/2=9 mm; sweep1=17 mm; sweep_2=9 mm; sweep_D=34 mm; sweep_H=535 mm; sweep_H1=74 mm; sweep_box1=50 mm; sweep_box2=22 mm
- DN500_PN10_Pilot range ( 5 - 10): Actuator_L=209 mm; Actuator_L1=188 mm; Actuator_d=59 mm; Body_H=429 mm; Body_Rib_L=179 mm; Bolt_Dia=44 mm; Bonnet_D=215 mm; Bonnet_D1=429 mm; Bonnet_R=450 mm; Bonnet_dim1=300 mm; Bonnet_dim1_H=53 mm; Bonnet_dim1_H1=669 mm; Bonnet_dim2=150 mm; Bonnet_dim3=113 mm; Bore=250 mm; Bore1=300 mm; Bore2=375 mm; Centre_D=100 mm; Centre_D1=80 mm; Centre_nut=75 mm; Conrol_dim.=255 mm; Control_dim1=23 mm; Control_dim2=135 mm; Control_dim3=11 mm  [stored 0.0360892 ft]; Control_dim4=386 mm; Control_dim5=30 mm  [stored 0.0984252 ft]; Control_dim6=36 mm  [stored 0.11811 ft]; Control_dim7=49 mm; D=358 mm; DN=500 mm; FL_T=32 mm; H3=1181 mm; H33=46 mm; H4=93 mm; L=1250 mm; L3=495 mm; Nut_Dim1=57 mm; Nut_Dim2=9 mm; Nut_T=25 mm  [stored 0.082021 ft]; Raised_R=43 mm; Raised_dis=4 mm  [stored 0.0131234 ft]; Sweep_R=26 mm; Thickness=19 mm  [stored 0.062336 ft]; Thickness1=23 mm; W=448 mm; W1=465 mm; W11=336 mm; W2=465 mm; W22=372 mm; Wd1=395 mm; Wd2=465 mm; centre=390 mm; dim1=186 mm; nut_dim=215 mm; sweep=37 mm; sweep/2=9 mm; sweep1=17 mm; sweep_2=9 mm; sweep_D=34 mm; sweep_H=535 mm; sweep_H1=74 mm; sweep_box1=50 mm; sweep_box2=22 mm
- DN500_PN10_Pilot range ( 0.3 - 1.5): Actuator_L=209 mm; Actuator_L1=188 mm; Actuator_d=59 mm; Body_H=429 mm; Body_Rib_L=179 mm; Bolt_Dia=44 mm; Bonnet_D=215 mm; Bonnet_D1=429 mm; Bonnet_R=450 mm; Bonnet_dim1=300 mm; Bonnet_dim1_H=53 mm; Bonnet_dim1_H1=669 mm; Bonnet_dim2=150 mm; Bonnet_dim3=113 mm; Bore=250 mm; Bore1=300 mm; Bore2=375 mm; Centre_D=100 mm; Centre_D1=80 mm; Centre_nut=75 mm; Conrol_dim.=255 mm; Control_dim1=23 mm; Control_dim2=135 mm; Control_dim3=11 mm  [stored 0.0360892 ft]; Control_dim4=386 mm; Control_dim5=30 mm  [stored 0.0984252 ft]; Control_dim6=36 mm  [stored 0.11811 ft]; Control_dim7=49 mm; D=358 mm; DN=500 mm; FL_T=27 mm; H3=1181 mm; H33=46 mm; H4=93 mm; L=1250 mm; L3=495 mm; Nut_Dim1=57 mm; Nut_Dim2=9 mm; Nut_T=21 mm; Raised_R=43 mm; Raised_dis=4 mm  [stored 0.0131234 ft]; Sweep_R=26 mm; Thickness=16 mm  [stored 0.0524934 ft]; Thickness1=19 mm  [stored 0.062336 ft]; W=448 mm; W1=465 mm; W11=336 mm; W2=465 mm; W22=372 mm; Wd1=395 mm; Wd2=465 mm; centre=390 mm; dim1=186 mm; nut_dim=215 mm; sweep=37 mm; sweep/2=9 mm; sweep1=17 mm; sweep_2=9 mm; sweep_D=34 mm; sweep_H=535 mm; sweep_H1=74 mm; sweep_box1=50 mm; sweep_box2=22 mm
- DN500_PN16_Pilot range ( 1.5 - 6): Actuator_L=209 mm; Actuator_L1=188 mm; Actuator_d=59 mm; Body_H=429 mm; Body_Rib_L=179 mm; Bolt_Dia=44 mm; Bonnet_D=215 mm; Bonnet_D1=429 mm; Bonnet_R=450 mm; Bonnet_dim1=300 mm; Bonnet_dim1_H=53 mm; Bonnet_dim1_H1=669 mm; Bonnet_dim2=150 mm; Bonnet_dim3=113 mm; Bore=250 mm; Bore1=300 mm; Bore2=375 mm; Centre_D=100 mm; Centre_D1=80 mm; Centre_nut=75 mm; Conrol_dim.=255 mm; Control_dim1=23 mm; Control_dim2=135 mm; Control_dim3=11 mm  [stored 0.0360892 ft]; Control_dim4=386 mm; Control_dim5=30 mm  [stored 0.0984252 ft]; Control_dim6=36 mm  [stored 0.11811 ft]; Control_dim7=49 mm; D=358 mm; DN=501 mm; FL_T=32 mm; H3=1181 mm; H33=46 mm; H4=93 mm; L=1250 mm; L3=495 mm; Nut_Dim1=57 mm; Nut_Dim2=9 mm; Nut_T=25 mm  [stored 0.082021 ft]; Raised_R=43 mm; Raised_dis=4 mm  [stored 0.0131234 ft]; Sweep_R=26 mm; Thickness=19 mm  [stored 0.062336 ft]; Thickness1=23 mm; W=448 mm; W1=465 mm; W11=336 mm; W2=465 mm; W22=372 mm; Wd1=395 mm; Wd2=465 mm; centre=390 mm; dim1=186 mm; nut_dim=215 mm; sweep=37 mm; sweep/2=9 mm; sweep1=17 mm; sweep_2=9 mm; sweep_D=34 mm; sweep_H=535 mm; sweep_H1=74 mm; sweep_box1=50 mm; sweep_box2=22 mm
- DN500_PN16_Pilot range ( 5 - 10): Actuator_L=209 mm; Actuator_L1=188 mm; Actuator_d=59 mm; Body_H=429 mm; Body_Rib_L=179 mm; Bolt_Dia=44 mm; Bonnet_D=215 mm; Bonnet_D1=429 mm; Bonnet_R=450 mm; Bonnet_dim1=300 mm; Bonnet_dim1_H=53 mm; Bonnet_dim1_H1=669 mm; Bonnet_dim2=150 mm; Bonnet_dim3=113 mm; Bore=250 mm; Bore1=300 mm; Bore2=376 mm; Centre_D=100 mm; Centre_D1=80 mm; Centre_nut=75 mm; Conrol_dim.=255 mm; Control_dim1=23 mm; Control_dim2=135 mm; Control_dim3=11 mm  [stored 0.0360892 ft]; Control_dim4=386 mm; Control_dim5=30 mm  [stored 0.0984252 ft]; Control_dim6=36 mm  [stored 0.11811 ft]; Control_dim7=49 mm; D=358 mm; DN=501 mm; FL_T=32 mm; H3=1181 mm; H33=46 mm; H4=93 mm; L=1250 mm; L3=495 mm; Nut_Dim1=57 mm; Nut_Dim2=9 mm; Nut_T=25 mm  [stored 0.082021 ft]; Raised_R=43 mm; Raised_dis=5 mm  [stored 0.0164042 ft]; Sweep_R=26 mm; Thickness=19 mm  [stored 0.062336 ft]; Thickness1=23 mm; W=448 mm; W1=465 mm; W11=336 mm; W2=465 mm; W22=372 mm; Wd1=395 mm; Wd2=465 mm; centre=391 mm; dim1=186 mm; nut_dim=215 mm; sweep=37 mm; sweep/2=9 mm; sweep1=17 mm; sweep_2=9 mm; sweep_D=34 mm; sweep_H=535 mm; sweep_H1=74 mm; sweep_box1=50 mm; sweep_box2=22 mm
- DN500_PN16_Pilot range ( 10 - 16): Actuator_L=209 mm; Actuator_L1=188 mm; Actuator_d=59 mm; Body_H=429 mm; Body_Rib_L=179 mm; Bolt_Dia=44 mm; Bonnet_D=215 mm; Bonnet_D1=429 mm; Bonnet_R=450 mm; Bonnet_dim1=300 mm; Bonnet_dim1_H=53 mm; Bonnet_dim1_H1=669 mm; Bonnet_dim2=150 mm; Bonnet_dim3=113 mm; Bore=250 mm; Bore1=300 mm; Bore2=375 mm; Centre_D=100 mm; Centre_D1=80 mm; Centre_nut=75 mm; Conrol_dim.=255 mm; Control_dim1=23 mm; Control_dim2=135 mm; Control_dim3=11 mm  [stored 0.0360892 ft]; Control_dim4=386 mm; Control_dim5=30 mm  [stored 0.0984252 ft]; Control_dim6=36 mm  [stored 0.11811 ft]; Control_dim7=49 mm; D=358 mm; DN=501 mm; FL_T=32 mm; H3=1181 mm; H33=46 mm; H4=93 mm; L=1250 mm; L3=495 mm; Nut_Dim1=57 mm; Nut_Dim2=9 mm; Nut_T=25 mm  [stored 0.082021 ft]; Raised_R=43 mm; Raised_dis=4 mm  [stored 0.0131234 ft]; Sweep_R=26 mm; Thickness=19 mm  [stored 0.062336 ft]; Thickness1=23 mm; W=448 mm; W1=465 mm; W11=336 mm; W2=465 mm; W22=372 mm; Wd1=395 mm; Wd2=465 mm; centre=390 mm; dim1=186 mm; nut_dim=215 mm; sweep=37 mm; sweep/2=9 mm; sweep1=17 mm; sweep_2=9 mm; sweep_D=34 mm; sweep_H=535 mm; sweep_H1=74 mm; sweep_box1=50 mm; sweep_box2=22 mm
- DN500_PN16_Pilot range ( 0.3 - 1.5): Actuator_L=209 mm; Actuator_L1=188 mm; Actuator_d=59 mm; Body_H=429 mm; Body_Rib_L=179 mm; Bolt_Dia=44 mm; Bonnet_D=215 mm; Bonnet_D1=429 mm; Bonnet_R=450 mm; Bonnet_dim1=300 mm; Bonnet_dim1_H=53 mm; Bonnet_dim1_H1=669 mm; Bonnet_dim2=150 mm; Bonnet_dim3=113 mm; Bore=250 mm; Bore1=300 mm; Bore2=375 mm; Centre_D=100 mm; Centre_D1=80 mm; Centre_nut=75 mm; Conrol_dim.=255 mm; Control_dim1=23 mm; Control_dim2=135 mm; Control_dim3=11 mm  [stored 0.0360892 ft]; Control_dim4=386 mm; Control_dim5=30 mm  [stored 0.0984252 ft]; Control_dim6=36 mm  [stored 0.11811 ft]; Control_dim7=49 mm; D=358 mm; DN=500 mm; FL_T=32 mm; H3=1181 mm; H33=46 mm; H4=93 mm; L=1250 mm; L3=495 mm; Nut_Dim1=57 mm; Nut_Dim2=9 mm; Nut_T=25 mm  [stored 0.082021 ft]; Raised_R=43 mm; Raised_dis=4 mm  [stored 0.0131234 ft]; Sweep_R=26 mm; Thickness=19 mm  [stored 0.062336 ft]; Thickness1=23 mm; W=448 mm; W1=465 mm; W11=336 mm; W2=465 mm; W22=372 mm; Wd1=395 mm; Wd2=465 mm; centre=390 mm; dim1=186 mm; nut_dim=215 mm; sweep=37 mm; sweep/2=9 mm; sweep1=17 mm; sweep_2=9 mm; sweep_D=34 mm; sweep_H=535 mm; sweep_H1=74 mm; sweep_box1=50 mm; sweep_box2=22 mm
- DN600_PN10_Pilot range ( 0.3 - 1.5): Actuator_L=229 mm; Actuator_L1=206 mm; Actuator_d=69 mm; Body_H=504 mm; Body_Rib_L=210 mm; Bolt_Dia=44 mm; Bonnet_D=252 mm; Bonnet_D1=504 mm; Bonnet_R=529 mm; Bonnet_dim1=353 mm; Bonnet_dim1_H=31 mm; Bonnet_dim1_H1=707 mm; Bonnet_dim2=176 mm; Bonnet_dim3=132 mm; Bore=300 mm; Bore1=360 mm; Bore2=450 mm; Centre_D=100 mm; Centre_D1=80 mm; Centre_nut=75 mm; Conrol_dim.=300 mm; Control_dim1=26 mm; Control_dim2=159 mm; Control_dim3=13 mm; Control_dim4=454 mm; Control_dim5=36 mm  [stored 0.11811 ft]; Control_dim6=43 mm; Control_dim7=58 mm; D=420 mm; DN=600 mm; FL_T=30 mm  [stored 0.0984252 ft]; H3=1290 mm; H33=49 mm; H4=98 mm; L=1450 mm; L3=582 mm; Nut_Dim1=57 mm; Nut_Dim2=11 mm  [stored 0.0360892 ft]; Nut_T=24 mm  [stored 0.0787402 ft]; Raised_R=48 mm; Raised_dis=5 mm  [stored 0.0164042 ft]; Sweep_R=26 mm; Thickness=18 mm  [stored 0.0590551 ft]; Thickness1=22 mm; W=492 mm; W1=509 mm; W11=371 mm; W2=509 mm; W22=407 mm; Wd1=433 mm; Wd2=509 mm; centre=468 mm; dim1=204 mm; nut_dim=252 mm; sweep=37 mm; sweep/2=9 mm; sweep1=17 mm; sweep_2=9 mm; sweep_D=34 mm; sweep_H=566 mm; sweep_H1=43 mm; sweep_box1=50 mm; sweep_box2=22 mm
- DN600_PN10_Pilot range ( 5 - 10): Actuator_L=229 mm; Actuator_L1=206 mm; Actuator_d=69 mm; Body_H=504 mm; Body_Rib_L=210 mm; Bolt_Dia=44 mm; Bonnet_D=252 mm; Bonnet_D1=504 mm; Bonnet_R=529 mm; Bonnet_dim1=353 mm; Bonnet_dim1_H=31 mm; Bonnet_dim1_H1=707 mm; Bonnet_dim2=176 mm; Bonnet_dim3=132 mm; Bore=300 mm; Bore1=360 mm; Bore2=450 mm; Centre_D=100 mm; Centre_D1=80 mm; Centre_nut=75 mm; Conrol_dim.=300 mm; Control_dim1=26 mm; Control_dim2=159 mm; Control_dim3=13 mm; Control_dim4=454 mm; Control_dim5=36 mm  [stored 0.11811 ft]; Control_dim6=43 mm; Control_dim7=58 mm; D=420 mm; DN=600 mm; FL_T=30 mm  [stored 0.0984252 ft]; H3=1290 mm; H33=49 mm; H4=98 mm; L=1450 mm; L3=582 mm; Nut_Dim1=57 mm; Nut_Dim2=11 mm  [stored 0.0360892 ft]; Nut_T=24 mm  [stored 0.0787402 ft]; Raised_R=48 mm; Raised_dis=5 mm  [stored 0.0164042 ft]; Sweep_R=26 mm; Thickness=18 mm  [stored 0.0590551 ft]; Thickness1=22 mm; W=492 mm; W1=509 mm; W11=371 mm; W2=509 mm; W22=407 mm; Wd1=433 mm; Wd2=509 mm; centre=468 mm; dim1=204 mm; nut_dim=252 mm; sweep=37 mm; sweep/2=9 mm; sweep1=17 mm; sweep_2=9 mm; sweep_D=34 mm; sweep_H=566 mm; sweep_H1=43 mm; sweep_box1=50 mm; sweep_box2=22 mm
- DN600_PN10_Pilot range ( 1.5 - 6): Actuator_L=229 mm; Actuator_L1=206 mm; Actuator_d=69 mm; Body_H=504 mm; Body_Rib_L=210 mm; Bolt_Dia=44 mm; Bonnet_D=252 mm; Bonnet_D1=504 mm; Bonnet_R=529 mm; Bonnet_dim1=353 mm; Bonnet_dim1_H=31 mm; Bonnet_dim1_H1=707 mm; Bonnet_dim2=176 mm; Bonnet_dim3=132 mm; Bore=300 mm; Bore1=360 mm; Bore2=450 mm; Centre_D=100 mm; Centre_D1=80 mm; Centre_nut=75 mm; Conrol_dim.=300 mm; Control_dim1=26 mm; Control_dim2=159 mm; Control_dim3=13 mm; Control_dim4=454 mm; Control_dim5=36 mm  [stored 0.11811 ft]; Control_dim6=43 mm; Control_dim7=58 mm; D=420 mm; DN=600 mm; FL_T=36 mm  [stored 0.11811 ft]; H3=1290 mm; H33=49 mm; H4=98 mm; L=1450 mm; L3=582 mm; Nut_Dim1=57 mm; Nut_Dim2=11 mm  [stored 0.0360892 ft]; Nut_T=29 mm; Raised_R=48 mm; Raised_dis=5 mm  [stored 0.0164042 ft]; Sweep_R=26 mm; Thickness=22 mm; Thickness1=26 mm; W=492 mm; W1=509 mm; W11=371 mm; W2=509 mm; W22=407 mm; Wd1=433 mm; Wd2=509 mm; centre=468 mm; dim1=204 mm; nut_dim=252 mm; sweep=37 mm; sweep/2=9 mm; sweep1=17 mm; sweep_2=9 mm; sweep_D=34 mm; sweep_H=566 mm; sweep_H1=43 mm; sweep_box1=50 mm; sweep_box2=22 mm
- DN600_PN16_Pilot range ( 1.5 - 6): Actuator_L=229 mm; Actuator_L1=206 mm; Actuator_d=69 mm; Body_H=504 mm; Body_Rib_L=210 mm; Bolt_Dia=44 mm; Bonnet_D=252 mm; Bonnet_D1=504 mm; Bonnet_R=529 mm; Bonnet_dim1=353 mm; Bonnet_dim1_H=31 mm; Bonnet_dim1_H1=707 mm; Bonnet_dim2=176 mm; Bonnet_dim3=132 mm; Bore=300 mm; Bore1=360 mm; Bore2=450 mm; Centre_D=100 mm; Centre_D1=80 mm; Centre_nut=75 mm; Conrol_dim.=300 mm; Control_dim1=26 mm; Control_dim2=159 mm; Control_dim3=13 mm; Control_dim4=454 mm; Control_dim5=36 mm  [stored 0.11811 ft]; Control_dim6=43 mm; Control_dim7=58 mm; D=420 mm; DN=601 mm; FL_T=36 mm  [stored 0.11811 ft]; H3=1290 mm; H33=49 mm; H4=98 mm; L=1450 mm; L3=582 mm; Nut_Dim1=57 mm; Nut_Dim2=11 mm  [stored 0.0360892 ft]; Nut_T=29 mm; Raised_R=48 mm; Raised_dis=5 mm  [stored 0.0164042 ft]; Sweep_R=26 mm; Thickness=22 mm; Thickness1=26 mm; W=492 mm; W1=509 mm; W11=371 mm; W2=509 mm; W22=407 mm; Wd1=433 mm; Wd2=509 mm; centre=468 mm; dim1=204 mm; nut_dim=252 mm; sweep=37 mm; sweep/2=9 mm; sweep1=17 mm; sweep_2=9 mm; sweep_D=34 mm; sweep_H=566 mm; sweep_H1=43 mm; sweep_box1=50 mm; sweep_box2=22 mm
- DN600_PN16_Pilot range ( 5 - 10): Actuator_L=229 mm; Actuator_L1=206 mm; Actuator_d=69 mm; Body_H=504 mm; Body_Rib_L=210 mm; Bolt_Dia=44 mm; Bonnet_D=252 mm; Bonnet_D1=504 mm; Bonnet_R=529 mm; Bonnet_dim1=353 mm; Bonnet_dim1_H=31 mm; Bonnet_dim1_H1=707 mm; Bonnet_dim2=176 mm; Bonnet_dim3=132 mm; Bore=300 mm; Bore1=360 mm; Bore2=451 mm; Centre_D=100 mm; Centre_D1=80 mm; Centre_nut=75 mm; Conrol_dim.=300 mm; Control_dim1=26 mm; Control_dim2=159 mm; Control_dim3=13 mm; Control_dim4=454 mm; Control_dim5=36 mm  [stored 0.11811 ft]; Control_dim6=43 mm; Control_dim7=58 mm; D=420 mm; DN=601 mm; FL_T=36 mm  [stored 0.11811 ft]; H3=1290 mm; H33=49 mm; H4=98 mm; L=1450 mm; L3=582 mm; Nut_Dim1=57 mm; Nut_Dim2=11 mm  [stored 0.0360892 ft]; Nut_T=29 mm; Raised_R=48 mm; Raised_dis=5 mm  [stored 0.0164042 ft]; Sweep_R=26 mm; Thickness=22 mm; Thickness1=26 mm; W=492 mm; W1=509 mm; W11=371 mm; W2=509 mm; W22=407 mm; Wd1=433 mm; Wd2=509 mm; centre=469 mm; dim1=204 mm; nut_dim=252 mm; sweep=37 mm; sweep/2=9 mm; sweep1=17 mm; sweep_2=9 mm; sweep_D=34 mm; sweep_H=566 mm; sweep_H1=43 mm; sweep_box1=50 mm; sweep_box2=22 mm
- DN600_PN16_Pilot range ( 10 - 16): Actuator_L=229 mm; Actuator_L1=206 mm; Actuator_d=69 mm; Body_H=504 mm; Body_Rib_L=210 mm; Bolt_Dia=44 mm; Bonnet_D=252 mm; Bonnet_D1=504 mm; Bonnet_R=529 mm; Bonnet_dim1=353 mm; Bonnet_dim1_H=31 mm; Bonnet_dim1_H1=707 mm; Bonnet_dim2=176 mm; Bonnet_dim3=132 mm; Bore=300 mm; Bore1=360 mm; Bore2=450 mm; Centre_D=100 mm; Centre_D1=80 mm; Centre_nut=75 mm; Conrol_dim.=300 mm; Control_dim1=26 mm; Control_dim2=159 mm; Control_dim3=13 mm; Control_dim4=454 mm; Control_dim5=36 mm  [stored 0.11811 ft]; Control_dim6=43 mm; Control_dim7=58 mm; D=420 mm; DN=601 mm; FL_T=36 mm  [stored 0.11811 ft]; H3=1290 mm; H33=49 mm; H4=98 mm; L=1450 mm; L3=582 mm; Nut_Dim1=57 mm; Nut_Dim2=11 mm  [stored 0.0360892 ft]; Nut_T=29 mm; Raised_R=48 mm; Raised_dis=5 mm  [stored 0.0164042 ft]; Sweep_R=26 mm; Thickness=22 mm; Thickness1=26 mm; W=492 mm; W1=509 mm; W11=371 mm; W2=509 mm; W22=407 mm; Wd1=433 mm; Wd2=509 mm; centre=468 mm; dim1=204 mm; nut_dim=252 mm; sweep=37 mm; sweep/2=9 mm; sweep1=17 mm; sweep_2=9 mm; sweep_D=34 mm; sweep_H=566 mm; sweep_H1=43 mm; sweep_box1=50 mm; sweep_box2=22 mm
- DN600_PN16_Pilot range ( 0.3 - 1.5): Actuator_L=229 mm; Actuator_L1=206 mm; Actuator_d=69 mm; Body_H=504 mm; Body_Rib_L=210 mm; Bolt_Dia=44 mm; Bonnet_D=252 mm; Bonnet_D1=504 mm; Bonnet_R=529 mm; Bonnet_dim1=353 mm; Bonnet_dim1_H=31 mm; Bonnet_dim1_H1=707 mm; Bonnet_dim2=176 mm; Bonnet_dim3=132 mm; Bore=300 mm; Bore1=360 mm; Bore2=450 mm; Centre_D=100 mm; Centre_D1=80 mm; Centre_nut=75 mm; Conrol_dim.=300 mm; Control_dim1=26 mm; Control_dim2=159 mm; Control_dim3=13 mm; Control_dim4=454 mm; Control_dim5=36 mm  [stored 0.11811 ft]; Control_dim6=43 mm; Control_dim7=58 mm; D=420 mm; DN=600 mm; FL_T=36 mm  [stored 0.11811 ft]; H3=1290 mm; H33=49 mm; H4=98 mm; L=1450 mm; L3=582 mm; Nut_Dim1=57 mm; Nut_Dim2=11 mm  [stored 0.0360892 ft]; Nut_T=29 mm; Raised_R=48 mm; Raised_dis=5 mm  [stored 0.0164042 ft]; Sweep_R=26 mm; Thickness=22 mm; Thickness1=26 mm; W=492 mm; W1=509 mm; W11=371 mm; W2=509 mm; W22=407 mm; Wd1=433 mm; Wd2=509 mm; centre=468 mm; dim1=204 mm; nut_dim=252 mm; sweep=37 mm; sweep/2=9 mm; sweep1=17 mm; sweep_2=9 mm; sweep_D=34 mm; sweep_H=566 mm; sweep_H1=43 mm; sweep_box1=50 mm; sweep_box2=22 mm

note: [stored X ft] marks values corroborated as IEEE doubles in the binary element streams (Revit-internal decimal feet)

## geometry (parser evidence)
native form markers: Sweep x9
no freeform markers — native parametric forms only
